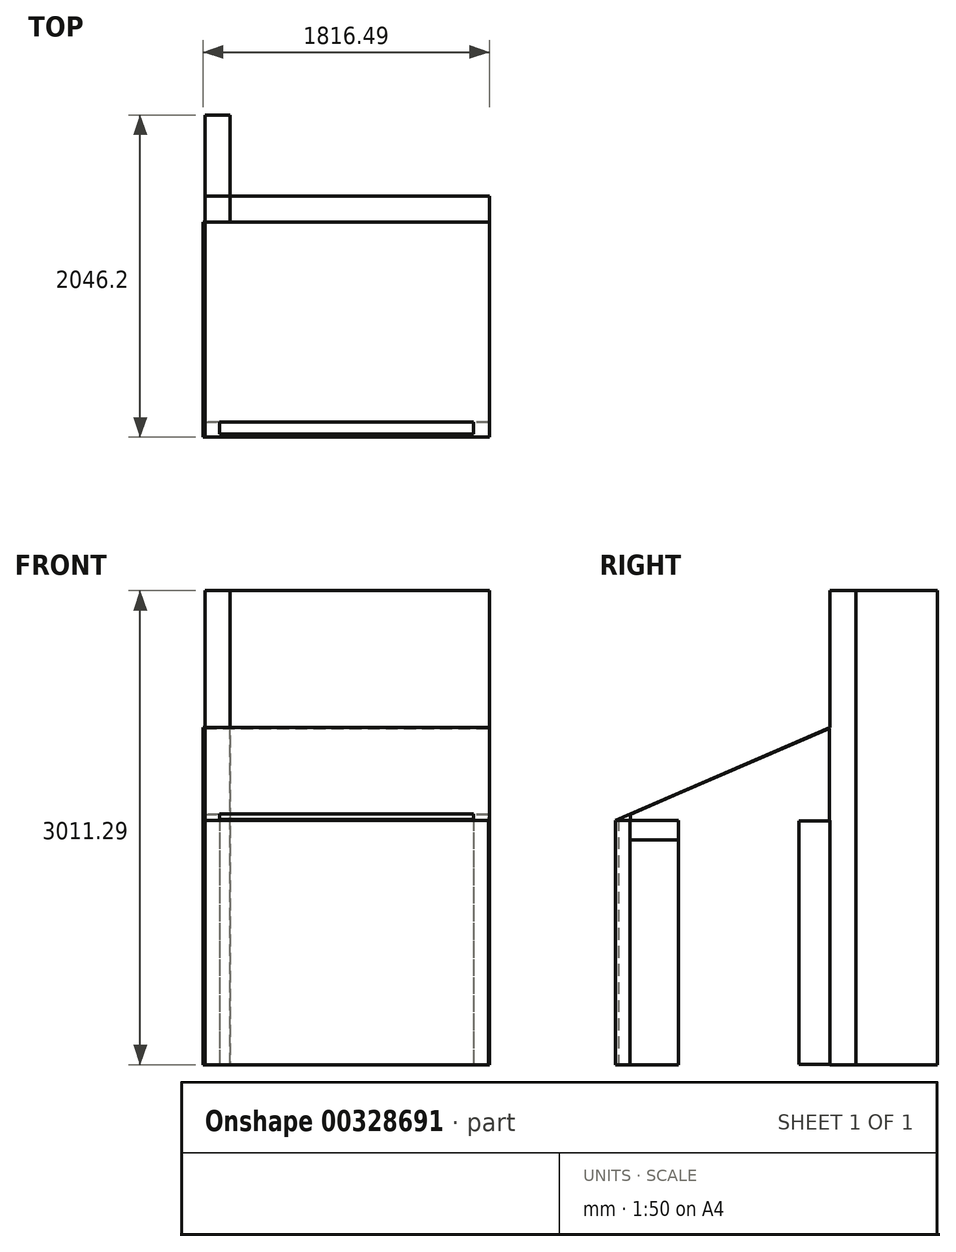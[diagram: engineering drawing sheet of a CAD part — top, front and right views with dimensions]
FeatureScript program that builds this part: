
annotation { "Feature Type Name" : "Feature", "Feature Type Description" : "" }
export const myFeature = defineFeature(function(context is Context, id is Id, definition is map)
    precondition{}
    {
        {
            var Q0;
            Q0=qCreatedBy(makeId("Right.planeOp"),FACE);
            var sketch = newSketch(context, id + "F0", { "sketchPlane" : qUnion([Q0])});
            skLineSegment(sketch, "E0.bottom", {"start": v(0, -290) * mm, "end": v(-95, -290) * mm});
            skLineSegment(sketch, "E0.left", {"start": v(0, -290) * mm, "end": v(0, 1300) * mm});
            skLineSegment(sketch, "E0.right", {"start": v(-95, -290) * mm, "end": v(-95, 1260) * mm});
            skLineSegment(sketch, "E1", {"start": v(-95, 1260) * mm, "end": v(-95, 1260) * mm});
            skLineSegment(sketch, "E2", {"start": v(0, 1300) * mm, "end": v(-95, 1260) * mm});
            skSolve(sketch);
        }
        {
            var Q0;
            Q0 = qSketchRegion(id + "F0", true);
            extrude(context, id + "F1", {"entities" : qUnion([Q0]), "depth" : 1800 * mm});
        }
        {
            var Q0;
            Q0=makeQuery(id+"F1.opExtrude","CAP_FACE",FACE,{"disambiguationData":[OSD([sQuery(id+"F0.wireOp",EDGE,"E0.bottom"),sQuery(id+"F0.wireOp",EDGE,"E0.left"),sQuery(id+"F0.wireOp",EDGE,"E0.right"),sQuery(id+"F0.wireOp",EDGE,"E2")])],"isStart":true});
            var sketch = newSketch(context, id + "F2", { "sketchPlane" : qUnion([Q0])});
            skPoint(sketch, "E3.end.orphan", {"position": v(95, -821.41) * mm});
            skPoint(sketch, "E3.start.orphan", {"position": v(-1270, -821.41) * mm});
            skLineSegment(sketch, "E4", {"start": v(-1270, -290) * mm, "end": v(-1270, 2721) * mm});
            skLineSegment(sketch, "E5", {"start": v(-1270, 2721) * mm, "end": v(-1951.2, 2721) * mm});
            skLineSegment(sketch, "E6", {"start": v(-1951.2, 2721) * mm, "end": v(-1951.2, -290) * mm});
            skLineSegment(sketch, "E7", {"start": v(-1951.2, -290) * mm, "end": v(-1270, -290) * mm});
            skLineSegment(sketch, "E8", {"start": v(95, 1260) * mm, "end": v(-1270, 1852.83) * mm});
            skPoint(sketch, "E9.end.orphan", {"position": v(-587.5, -290) * mm});
            skPoint(sketch, "E10.orphan", {"position": v(95, -290) * mm});
            skLineSegment(sketch, "E11", {"start": v(95, 1260) * mm, "end": v(0, 1260) * mm});
            skLineSegment(sketch, "E12", {"start": v(0, 1260) * mm, "end": v(-1270, 1260) * mm});
            skSolve(sketch);
        }
        {
            var Q0;
            {var subQ0=sQuery(id+"F2.wireOp",EDGE,"E11");Q0=makeQuery(id+"F2.imprint","IMPRINT",FACE,{"disambiguationData":[TD([[makeQuery(id+"F2.imprint","IMPRINT",EDGE,{"derivedFrom":subQ0}),1.0]])]});}
            var sketch = newSketch(context, id + "F3", { "sketchPlane" : qUnion([Q0])});
            skPoint(sketch, "E13.start.orphan", {"position": v(-1269.2, 1262.92) * mm});
            skLineSegment(sketch, "E14", {"start": v(-1270.6, 1381.92) * mm, "end": v(-1269.2, 1262.92) * mm});
            skPoint(sketch, "E15.end.orphan", {"position": v(-1302.17, 1381.92) * mm});
            skPoint(sketch, "E15.start.orphan", {"position": v(-1302.17, 1262.92) * mm});
            skLineSegment(sketch, "E16", {"start": v(-1270.6, 1381.92) * mm, "end": v(-1272, 1500.92) * mm});
            skLineSegment(sketch, "E17", {"start": v(-1272, 1500.92) * mm, "end": v(-1272, 1619.92) * mm});
            skLineSegment(sketch, "E18", {"start": v(-1272, 1619.92) * mm, "end": v(-1272, 1738.92) * mm});
            skLineSegment(sketch, "E19", {"start": v(-1272, 1738.92) * mm, "end": v(-1272, 1857.92) * mm});
            skLineSegment(sketch, "E20", {"start": v(-1269.2, 1262.92) * mm, "end": v(0, 1262.92) * mm});
            skLineSegment(sketch, "E21", {"start": v(0, 1262.92) * mm, "end": v(0, 1307.88) * mm});
            skLineSegment(sketch, "E22", {"start": v(-1272, 1857.92) * mm, "end": v(0, 1307.88) * mm});
            skLineSegment(sketch, "E23", {"start": v(-1270.6, 1381.92) * mm, "end": v(-171.23, 1381.92) * mm});
            skLineSegment(sketch, "E24", {"start": v(-1272, 1500.92) * mm, "end": v(-446.4, 1500.92) * mm});
            skLineSegment(sketch, "E25", {"start": v(-1272, 1619.92) * mm, "end": v(-721.6, 1619.92) * mm});
            skLineSegment(sketch, "E26", {"start": v(-1272, 1738.92) * mm, "end": v(-996.8, 1738.92) * mm});
            skLineSegment(sketch, "E27", {"start": v(334.75, -589.34) * mm, "end": v(334.75, -589.34) * mm});
            skLineSegment(sketch, "E28", {"start": v(95, -290.3) * mm, "end": v(-305, -290.3) * mm});
            skPoint(sketch, "E29.end.orphan", {"position": v(-505, -589.34) * mm});
            skLineSegment(sketch, "E30", {"start": v(-305, -290.3) * mm, "end": v(-305, 1262.92) * mm});
            skPoint(sketch, "E31.start.orphan", {"position": v(95, -622.61) * mm});
            skPoint(sketch, "E32.orphan", {"position": v(-505, -290.3) * mm});
            skLineSegment(sketch, "E33", {"start": v(95, -290.3) * mm, "end": v(95, -171.3) * mm});
            skLineSegment(sketch, "E34", {"start": v(95, -171.3) * mm, "end": v(95, -52.3) * mm});
            skLineSegment(sketch, "E35", {"start": v(95, -52.3) * mm, "end": v(95, 66.7) * mm});
            skLineSegment(sketch, "E36", {"start": v(95, 66.7) * mm, "end": v(95, 185.7) * mm});
            skLineSegment(sketch, "E37", {"start": v(95, 185.7) * mm, "end": v(95, 304.7) * mm});
            skLineSegment(sketch, "E38", {"start": v(95, 304.7) * mm, "end": v(95, 423.7) * mm});
            skLineSegment(sketch, "E39", {"start": v(95, 423.7) * mm, "end": v(95, 542.7) * mm});
            skLineSegment(sketch, "E40", {"start": v(95, 542.7) * mm, "end": v(95, 661.7) * mm});
            skLineSegment(sketch, "E41", {"start": v(95, 661.7) * mm, "end": v(95, 780.7) * mm});
            skLineSegment(sketch, "E42", {"start": v(95, 780.7) * mm, "end": v(95, 899.7) * mm});
            skLineSegment(sketch, "E43", {"start": v(95, 899.7) * mm, "end": v(95, 1018.7) * mm});
            skLineSegment(sketch, "E44", {"start": v(95, 1018.7) * mm, "end": v(95, 1137.7) * mm});
            skLineSegment(sketch, "E45", {"start": v(95, 1137.7) * mm, "end": v(95, 1256.7) * mm});
            skLineSegment(sketch, "E46", {"start": v(95, 1137.7) * mm, "end": v(-305, 1137.7) * mm});
            skLineSegment(sketch, "E47", {"start": v(95, 1018.7) * mm, "end": v(-305, 1018.7) * mm});
            skLineSegment(sketch, "E48", {"start": v(95, 899.7) * mm, "end": v(-305, 899.7) * mm});
            skLineSegment(sketch, "E49", {"start": v(95, 780.7) * mm, "end": v(-305, 780.7) * mm});
            skLineSegment(sketch, "E50", {"start": v(95, 661.7) * mm, "end": v(-305, 661.7) * mm});
            skLineSegment(sketch, "E51", {"start": v(95, 542.7) * mm, "end": v(-305, 542.7) * mm});
            skPoint(sketch, "E51.endSnap0", {"position": v(-305, 486.31) * mm});
            skLineSegment(sketch, "E52", {"start": v(95, 423.7) * mm, "end": v(-305, 423.7) * mm});
            skLineSegment(sketch, "E53", {"start": v(95, 304.7) * mm, "end": v(-305, 304.7) * mm});
            skLineSegment(sketch, "E54", {"start": v(95, 185.7) * mm, "end": v(-305, 185.7) * mm});
            skLineSegment(sketch, "E55", {"start": v(95, 66.7) * mm, "end": v(-305, 66.7) * mm});
            skLineSegment(sketch, "E56", {"start": v(95, -52.3) * mm, "end": v(-305, -52.3) * mm});
            skLineSegment(sketch, "E57", {"start": v(95, -171.3) * mm, "end": v(-305, -171.3) * mm});
            skLineSegment(sketch, "E58", {"start": v(-1270.61, -288.9) * mm, "end": v(-1070.61, -288.9) * mm});
            skLineSegment(sketch, "E59", {"start": v(-1070.61, -288.9) * mm, "end": v(-1070.61, 1262.92) * mm});
            skLineSegment(sketch, "E60", {"start": v(-1269.2, 1262.92) * mm, "end": v(-1269.2, 0) * mm});
            skLineSegment(sketch, "E61", {"start": v(-1269.2, 0) * mm, "end": v(-1270.61, -288.9) * mm});
            skLineSegment(sketch, "E62", {"start": v(-1070.61, -171.3) * mm, "end": v(-1270.04, -171.3) * mm});
            skLineSegment(sketch, "E63", {"start": v(-1070.61, -52.3) * mm, "end": v(-1269.46, -52.3) * mm});
            skLineSegment(sketch, "E64", {"start": v(-1070.61, 66.7) * mm, "end": v(-1269.2, 66.7) * mm});
            skLineSegment(sketch, "E65", {"start": v(-305, 185.7) * mm, "end": v(-305, 185.7) * mm});
            skLineSegment(sketch, "E66", {"start": v(-1070.61, 185.7) * mm, "end": v(-1269.2, 185.7) * mm});
            skLineSegment(sketch, "E67", {"start": v(-1070.61, 304.7) * mm, "end": v(-1269.2, 304.7) * mm});
            skLineSegment(sketch, "E68", {"start": v(-1070.61, 423.7) * mm, "end": v(-1269.2, 423.7) * mm});
            skLineSegment(sketch, "E69", {"start": v(-1070.61, 542.7) * mm, "end": v(-1269.2, 542.7) * mm});
            skPoint(sketch, "E69.endSnap0", {"position": v(-1269.2, 631.46) * mm});
            skLineSegment(sketch, "E70", {"start": v(-1070.61, 661.7) * mm, "end": v(-1269.2, 661.7) * mm});
            skLineSegment(sketch, "E71", {"start": v(-1070.61, 780.7) * mm, "end": v(-1269.2, 780.7) * mm});
            skLineSegment(sketch, "E72", {"start": v(-1070.61, 899.7) * mm, "end": v(-1269.2, 899.7) * mm});
            skLineSegment(sketch, "E73", {"start": v(-1070.61, 1018.7) * mm, "end": v(-1269.2, 1018.7) * mm});
            skLineSegment(sketch, "E74", {"start": v(-1070.61, 1137.7) * mm, "end": v(-1269.2, 1137.7) * mm});
            skSolve(sketch);
        }
        {
            var Q0;
            {var subQ2=sQuery(id+"F2.wireOp",EDGE,"E8");Q0=makeQuery(id+"F2.imprint","IMPRINT",FACE,{"disambiguationData":[TD([[makeQuery(id+"F2.imprint","IMPRINT",EDGE,{"derivedFrom":subQ2}),1.0]])]});}
            var Q1;
            {var subQ5=sQuery(id+"F3.wireOp",EDGE,"E74");Q1=makeQuery(id+"F3.imprint","IMPRINT",FACE,{"disambiguationData":[TD([[makeQuery(id+"F3.imprint","IMPRINT",EDGE,{"derivedFrom":subQ5}),-1.0]])]});}
            var Q2;
            {var subQ0=sQuery(id+"F3.wireOp",EDGE,"E71");Q2=makeQuery(id+"F3.imprint","IMPRINT",FACE,{"disambiguationData":[TD([[makeQuery(id+"F3.imprint","IMPRINT",EDGE,{"derivedFrom":subQ0}),-1.0]])]});}
            var Q3;
            {var subQ0=sQuery(id+"F3.wireOp",EDGE,"E73");Q3=makeQuery(id+"F3.imprint","IMPRINT",FACE,{"disambiguationData":[TD([[makeQuery(id+"F3.imprint","IMPRINT",EDGE,{"derivedFrom":subQ0}),-1.0]])]});}
            var Q4;
            {var subQ0=sQuery(id+"F3.wireOp",EDGE,"E72");Q4=makeQuery(id+"F3.imprint","IMPRINT",FACE,{"disambiguationData":[TD([[makeQuery(id+"F3.imprint","IMPRINT",EDGE,{"derivedFrom":subQ0}),-1.0]])]});}
            var Q5;
            {var subQ0=sQuery(id+"F3.wireOp",EDGE,"E69");Q5=makeQuery(id+"F3.imprint","IMPRINT",FACE,{"disambiguationData":[TD([[makeQuery(id+"F3.imprint","IMPRINT",EDGE,{"derivedFrom":subQ0}),-1.0]])]});}
            var Q6;
            {var subQ0=sQuery(id+"F3.wireOp",EDGE,"E70");Q6=makeQuery(id+"F3.imprint","IMPRINT",FACE,{"disambiguationData":[TD([[makeQuery(id+"F3.imprint","IMPRINT",EDGE,{"derivedFrom":subQ0}),-1.0]])]});}
            var Q7;
            {var subQ0=sQuery(id+"F3.wireOp",EDGE,"E68");Q7=makeQuery(id+"F3.imprint","IMPRINT",FACE,{"disambiguationData":[TD([[makeQuery(id+"F3.imprint","IMPRINT",EDGE,{"derivedFrom":subQ0}),-1.0]])]});}
            var Q8;
            {var subQ0=sQuery(id+"F3.wireOp",EDGE,"E67");Q8=makeQuery(id+"F3.imprint","IMPRINT",FACE,{"disambiguationData":[TD([[makeQuery(id+"F3.imprint","IMPRINT",EDGE,{"derivedFrom":subQ0}),-1.0]])]});}
            var Q9;
            {var subQ0=sQuery(id+"F3.wireOp",EDGE,"E66");Q9=makeQuery(id+"F3.imprint","IMPRINT",FACE,{"disambiguationData":[TD([[makeQuery(id+"F3.imprint","IMPRINT",EDGE,{"derivedFrom":subQ0}),-1.0]])]});}
            var Q10;
            {var subQ0=sQuery(id+"F3.wireOp",EDGE,"E64");Q10=makeQuery(id+"F3.imprint","IMPRINT",FACE,{"disambiguationData":[TD([[makeQuery(id+"F3.imprint","IMPRINT",EDGE,{"derivedFrom":subQ0}),-1.0]])]});}
            var Q11;
            {var subQ3=sQuery(id+"F3.wireOp",EDGE,"E63");Q11=makeQuery(id+"F3.imprint","IMPRINT",FACE,{"disambiguationData":[TD([[makeQuery(id+"F3.imprint","IMPRINT",EDGE,{"derivedFrom":subQ3}),-1.0]])]});}
            var Q12;
            {var subQ0=sQuery(id+"F3.wireOp",EDGE,"E62");Q12=makeQuery(id+"F3.imprint","IMPRINT",FACE,{"disambiguationData":[TD([[makeQuery(id+"F3.imprint","IMPRINT",EDGE,{"derivedFrom":subQ0}),-1.0]])]});}
            var Q13;
            {var subQ0=sQuery(id+"F3.wireOp",EDGE,"E58");Q13=makeQuery(id+"F3.imprint","IMPRINT",FACE,{"disambiguationData":[TD([[makeQuery(id+"F3.imprint","IMPRINT",EDGE,{"derivedFrom":subQ0}),1.0]])]});}
            var Q14;
            {var subQ3=sQuery(id+"F3.wireOp",EDGE,"E28");Q14=makeQuery(id+"F3.imprint","IMPRINT",FACE,{"disambiguationData":[TD([[makeQuery(id+"F3.imprint","IMPRINT",EDGE,{"derivedFrom":subQ3}),-1.0]])]});}
            var Q15;
            {var subQ0=sQuery(id+"F3.wireOp",EDGE,"E56");var subQ1=sQuery(id+"F3.wireOp",EDGE,"E30");var subQ2=makeQuery(id+"F3.imprint","INTERSECT",VERTEX,{"derivedFrom":[subQ1,subQ0]});Q15=makeQuery(id+"F3.imprint","IMPRINT",FACE,{"disambiguationData":[TD([[makeQuery(id+"F3.imprint","IMPRINT",EDGE,{"disambiguationData":[TD([[subQ2,1.0]])],"derivedFrom":subQ1}),-1.0]])]});}
            var Q16;
            {var subQ0=sQuery(id+"F3.wireOp",EDGE,"E55");var subQ1=sQuery(id+"F3.wireOp",EDGE,"E30");var subQ2=makeQuery(id+"F3.imprint","INTERSECT",VERTEX,{"derivedFrom":[subQ1,subQ0]});Q16=makeQuery(id+"F3.imprint","IMPRINT",FACE,{"disambiguationData":[TD([[makeQuery(id+"F3.imprint","IMPRINT",EDGE,{"disambiguationData":[TD([[subQ2,1.0]])],"derivedFrom":subQ1}),-1.0]])]});}
            var Q17;
            {var subQ0=sQuery(id+"F3.wireOp",EDGE,"E54");var subQ1=sQuery(id+"F3.wireOp",EDGE,"E30");var subQ2=makeQuery(id+"F3.imprint","INTERSECT",VERTEX,{"derivedFrom":[subQ1,subQ0]});Q17=makeQuery(id+"F3.imprint","IMPRINT",FACE,{"disambiguationData":[TD([[makeQuery(id+"F3.imprint","IMPRINT",EDGE,{"disambiguationData":[TD([[subQ2,1.0]])],"derivedFrom":subQ1}),-1.0]])]});}
            var Q18;
            {var subQ0=sQuery(id+"F3.wireOp",EDGE,"E53");var subQ1=sQuery(id+"F3.wireOp",EDGE,"E30");var subQ2=makeQuery(id+"F3.imprint","INTERSECT",VERTEX,{"derivedFrom":[subQ1,subQ0]});Q18=makeQuery(id+"F3.imprint","IMPRINT",FACE,{"disambiguationData":[TD([[makeQuery(id+"F3.imprint","IMPRINT",EDGE,{"disambiguationData":[TD([[subQ2,1.0]])],"derivedFrom":subQ1}),-1.0]])]});}
            var Q19;
            {var subQ0=sQuery(id+"F3.wireOp",EDGE,"E52");var subQ1=sQuery(id+"F3.wireOp",EDGE,"E30");var subQ2=makeQuery(id+"F3.imprint","INTERSECT",VERTEX,{"derivedFrom":[subQ1,subQ0]});Q19=makeQuery(id+"F3.imprint","IMPRINT",FACE,{"disambiguationData":[TD([[makeQuery(id+"F3.imprint","IMPRINT",EDGE,{"disambiguationData":[TD([[subQ2,1.0]])],"derivedFrom":subQ1}),-1.0]])]});}
            var Q20;
            {var subQ0=sQuery(id+"F3.wireOp",EDGE,"E51");var subQ1=sQuery(id+"F3.wireOp",EDGE,"E30");var subQ2=makeQuery(id+"F3.imprint","INTERSECT",VERTEX,{"derivedFrom":[subQ1,subQ0]});Q20=makeQuery(id+"F3.imprint","IMPRINT",FACE,{"disambiguationData":[TD([[makeQuery(id+"F3.imprint","IMPRINT",EDGE,{"disambiguationData":[TD([[subQ2,1.0]])],"derivedFrom":subQ1}),-1.0]])]});}
            var Q21;
            {var subQ0=sQuery(id+"F3.wireOp",EDGE,"E50");var subQ1=sQuery(id+"F3.wireOp",EDGE,"E30");var subQ2=makeQuery(id+"F3.imprint","INTERSECT",VERTEX,{"derivedFrom":[subQ1,subQ0]});Q21=makeQuery(id+"F3.imprint","IMPRINT",FACE,{"disambiguationData":[TD([[makeQuery(id+"F3.imprint","IMPRINT",EDGE,{"disambiguationData":[TD([[subQ2,1.0]])],"derivedFrom":subQ1}),-1.0]])]});}
            var Q22;
            {var subQ0=sQuery(id+"F3.wireOp",EDGE,"E48");var subQ1=sQuery(id+"F3.wireOp",EDGE,"E30");var subQ2=makeQuery(id+"F3.imprint","INTERSECT",VERTEX,{"derivedFrom":[subQ1,subQ0]});Q22=makeQuery(id+"F3.imprint","IMPRINT",FACE,{"disambiguationData":[TD([[makeQuery(id+"F3.imprint","IMPRINT",EDGE,{"disambiguationData":[TD([[subQ2,1.0]])],"derivedFrom":subQ1}),-1.0]])]});}
            var Q23;
            {var subQ0=sQuery(id+"F3.wireOp",EDGE,"E47");var subQ1=sQuery(id+"F3.wireOp",EDGE,"E30");var subQ2=makeQuery(id+"F3.imprint","INTERSECT",VERTEX,{"derivedFrom":[subQ1,subQ0]});Q23=makeQuery(id+"F3.imprint","IMPRINT",FACE,{"disambiguationData":[TD([[makeQuery(id+"F3.imprint","IMPRINT",EDGE,{"disambiguationData":[TD([[subQ2,1.0]])],"derivedFrom":subQ1}),-1.0]])]});}
            var Q24;
            {var subQ0=sQuery(id+"F3.wireOp",EDGE,"E49");var subQ1=sQuery(id+"F3.wireOp",EDGE,"E30");var subQ2=makeQuery(id+"F3.imprint","INTERSECT",VERTEX,{"derivedFrom":[subQ1,subQ0]});Q24=makeQuery(id+"F3.imprint","IMPRINT",FACE,{"disambiguationData":[TD([[makeQuery(id+"F3.imprint","IMPRINT",EDGE,{"disambiguationData":[TD([[subQ2,1.0]])],"derivedFrom":subQ1}),-1.0]])]});}
            var Q25;
            {var subQ0=sQuery(id+"F3.wireOp",EDGE,"E46");var subQ1=sQuery(id+"F3.wireOp",EDGE,"E30");var subQ2=makeQuery(id+"F3.imprint","INTERSECT",VERTEX,{"derivedFrom":[subQ1,subQ0]});Q25=makeQuery(id+"F3.imprint","IMPRINT",FACE,{"disambiguationData":[TD([[makeQuery(id+"F3.imprint","IMPRINT",EDGE,{"disambiguationData":[TD([[subQ2,1.0]])],"derivedFrom":subQ1}),-1.0]])]});}
            extrude(context, id + "F4", {"entities" : qUnion([Q0, Q1, Q2, Q3, Q4, Q5, Q6, Q7, Q8, Q9, Q10, Q11, Q12, Q13, Q14, Q15, Q16, Q17, Q18, Q19, Q20, Q21, Q22, Q23, Q24, Q25]), "depth" : 10 * mm});
        }
        {
            var Q0;
            Q0=makeQuery(id+"F4.opExtrude","CAP_FACE",FACE,{"disambiguationData":[OSD([sQuery(id+"F0.wireOp",EDGE,"E0.left"),sQuery(id+"F0.wireOp",EDGE,"E2"),sQuery(id+"F2.wireOp",EDGE,"E4"),sQuery(id+"F2.wireOp",EDGE,"E8"),sQuery(id+"F2.wireOp",EDGE,"E12")])],"isStart":false});
            var sketch = newSketch(context, id + "F5", { "sketchPlane" : qUnion([Q0])});
            skLineSegment(sketch, "E75", {"start": v(-305.24, 1137.73) * mm, "end": v(-305.24, 1260) * mm});
            skLineSegment(sketch, "E76", {"start": v(-305.24, 1260) * mm, "end": v(0, 1260) * mm});
            skLineSegment(sketch, "E77", {"start": v(0, 1260) * mm, "end": v(0, 1138.9) * mm});
            skLineSegment(sketch, "E78", {"start": v(0, 1138.9) * mm, "end": v(-305.24, 1137.73) * mm});
            skSolve(sketch);
        }
        {
            var Q0;
            Q0=makeQuery(id+"F5.imprint","IMPRINT",FACE,{"disambiguationData":[TD([[makeQuery(id+"F5.imprint","IMPRINT",EDGE,{"derivedFrom":sQuery(id+"F5.wireOp",EDGE,"E75")}),-1.0]])]});
            extrude(context, id + "F6", {"entities" : qUnion([Q0]), "operationType" : NewBodyOperationType.ADD, "oppositeDirection" : true, "depth" : 10 * mm});
        }
        {
            var Q0;
            {var subQ0=sQuery(id+"F2.wireOp",EDGE,"E5");Q0=makeQuery(id+"F2.imprint","IMPRINT",FACE,{"disambiguationData":[TD([[makeQuery(id+"F2.imprint","IMPRINT",EDGE,{"derivedFrom":subQ0}),1.0]])]});}
            var Q1;
            Q1 = qSketchRegion(id + "F2", true);
            extrude(context, id + "F7", {"entities" : qUnion([Q0, Q1]), "oppositeDirection" : true, "depth" : 1806.5 * mm});
        }
        {
            var Q0;
            Q0=makeQuery(id+"F7.opExtrude","CAP_FACE",FACE,{"disambiguationData":[OSD([sQuery(id+"F2.wireOp",EDGE,"E4"),sQuery(id+"F2.wireOp",EDGE,"E5"),sQuery(id+"F2.wireOp",EDGE,"E6"),sQuery(id+"F2.wireOp",EDGE,"E7"),sQuery(id+"F2.wireOp",EDGE,"E8"),sQuery(id+"F2.wireOp",EDGE,"E11"),sQuery(id+"F2.wireOp",EDGE,"E12")])],"isStart":false});
            var sketch = newSketch(context, id + "F8", { "sketchPlane" : qUnion([Q0])});
            skLineSegment(sketch, "E79", {"start": v(305.91, 1258.1) * mm, "end": v(305.91, 1261.87) * mm});
            skLineSegment(sketch, "E80.right", {"start": v(1266.17, 1261.87) * mm, "end": v(1266.17, 1289.45) * mm});
            skLineSegment(sketch, "E81", {"start": v(1266.17, 1289.45) * mm, "end": v(1266.17, 1648.2) * mm});
            skLineSegment(sketch, "E82", {"start": v(1266.17, 1648.2) * mm, "end": v(1266.17, 1648.2) * mm});
            skLineSegment(sketch, "E83", {"start": v(1266.17, 1648.2) * mm, "end": v(1266.17, 1803.9) * mm});
            skLineSegment(sketch, "E84", {"start": v(1266.17, 1803.9) * mm, "end": v(1266.17, 1803.9) * mm});
            skLineSegment(sketch, "E85", {"start": v(1266.17, 1803.9) * mm, "end": v(1266.17, 1846.34) * mm});
            skLineSegment(sketch, "E86", {"start": v(1266.17, 1846.34) * mm, "end": v(1266.17, 1846.34) * mm});
            skLineSegment(sketch, "E87", {"start": v(1266.17, 1846.34) * mm, "end": v(1266.17, 1849.95) * mm});
            skLineSegment(sketch, "E88", {"start": v(1266.17, 1846.34) * mm, "end": v(305.91, 1433.16) * mm});
            skLineSegment(sketch, "E89", {"start": v(305.91, 1258.1) * mm, "end": v(379.95, 1258.1) * mm});
            skLineSegment(sketch, "E90", {"start": v(379.95, 1258.1) * mm, "end": v(522.25, 1258.1) * mm});
            skLineSegment(sketch, "E91", {"start": v(522.25, 1258.1) * mm, "end": v(522.25, 1258.1) * mm});
            skLineSegment(sketch, "E92", {"start": v(522.25, 1258.1) * mm, "end": v(570.38, 1258.1) * mm});
            skLineSegment(sketch, "E93", {"start": v(570.38, 1258.1) * mm, "end": v(747.25, 1258.1) * mm});
            skLineSegment(sketch, "E94", {"start": v(305.91, 1433.16) * mm, "end": v(305.91, 1258.1) * mm});
            skLineSegment(sketch, "E95", {"start": v(916.76, 1258.1) * mm, "end": v(747.25, 1258.1) * mm});
            skLineSegment(sketch, "E96", {"start": v(916.76, 1258.1) * mm, "end": v(1097.19, 1258.1) * mm});
            skLineSegment(sketch, "E97", {"start": v(1097.19, 1258.1) * mm, "end": v(1266.17, 1258.1) * mm});
            skLineSegment(sketch, "E98", {"start": v(1266.17, 1261.87) * mm, "end": v(1266.17, 1258.1) * mm});
            skSolve(sketch);
        }
        {
            var Q0;
            Q0 = qSketchRegion(id + "F8", true);
            var Q1;
            {var subQ5=sQuery(id+"F8.wireOp",EDGE,"E80.right");Q1=makeQuery(id+"F8.imprint","IMPRINT",FACE,{"disambiguationData":[TD([[makeQuery(id+"F8.imprint","IMPRINT",EDGE,{"derivedFrom":subQ5}),1.0]])]});}
            extrude(context, id + "F9", {"entities" : qUnion([Q0, Q1]), "operationType" : NewBodyOperationType.REMOVE, "oppositeDirection" : true, "depth" : 2295.18 * mm});
        }
        {
            var Q0;
            Q0=makeQuery(id+"F7.opExtrude","CAP_FACE",FACE,{"disambiguationData":[OSD([sQuery(id+"F2.wireOp",EDGE,"E4"),sQuery(id+"F2.wireOp",EDGE,"E5"),sQuery(id+"F2.wireOp",EDGE,"E6"),sQuery(id+"F2.wireOp",EDGE,"E7"),sQuery(id+"F2.wireOp",EDGE,"E8"),sQuery(id+"F2.wireOp",EDGE,"E11"),sQuery(id+"F2.wireOp",EDGE,"E12")])],"isStart":false});
            var sketch = newSketch(context, id + "F10", { "sketchPlane" : qUnion([Q0])});
            skLineSegment(sketch, "E99", {"start": v(305.91, 1433.16) * mm, "end": v(202.21, 1388.12) * mm});
            skLineSegment(sketch, "E100", {"start": v(202.21, 1388.12) * mm, "end": v(8.54, 1304) * mm});
            skLineSegment(sketch, "E101", {"start": v(8.54, 1304) * mm, "end": v(8.54, 1304) * mm});
            skLineSegment(sketch, "E102", {"start": v(8.54, 1304) * mm, "end": v(0.9, 1300.68) * mm});
            skLineSegment(sketch, "E103", {"start": v(0.9, 1300.68) * mm, "end": v(0.9, 1253.51) * mm});
            skLineSegment(sketch, "E104", {"start": v(305.91, 1433.16) * mm, "end": v(305.91, 1253.51) * mm});
            skLineSegment(sketch, "E105", {"start": v(305.91, 1253.51) * mm, "end": v(0.9, 1253.51) * mm});
            skSolve(sketch);
        }
        {
            var Q0;
            {var subQ7=sQuery(id+"F10.wireOp",EDGE,"E99");Q0=makeQuery(id+"F10.imprint","IMPRINT",FACE,{"disambiguationData":[TD([[makeQuery(id+"F10.imprint","IMPRINT",EDGE,{"derivedFrom":subQ7}),1.0]])]});}
            extrude(context, id + "F11", {"entities" : qUnion([Q0]), "operationType" : NewBodyOperationType.REMOVE, "oppositeDirection" : true, "depth" : 1985.6 * mm});
        }
        {
            var Q0;
            {var subQ0=sQuery(id+"F2.wireOp",EDGE,"E5");Q0=makeQuery(id+"F2.imprint","IMPRINT",FACE,{"disambiguationData":[TD([[makeQuery(id+"F2.imprint","IMPRINT",EDGE,{"derivedFrom":subQ0}),1.0]])]});}
            var sketch = newSketch(context, id + "F12", { "sketchPlane" : qUnion([Q0])});
            skLineSegment(sketch, "E106.bottom", {"start": v(-2153.87, -657.47) * mm, "end": v(-1434.67, -657.47) * mm});
            skLineSegment(sketch, "E106.top", {"start": v(-2153.87, 3181.57) * mm, "end": v(-1434.67, 3181.57) * mm});
            skLineSegment(sketch, "E106.left", {"start": v(-2153.87, -657.47) * mm, "end": v(-2153.87, 3181.57) * mm});
            skLineSegment(sketch, "E106.right", {"start": v(-1434.67, -657.47) * mm, "end": v(-1434.67, 3181.57) * mm});
            skSolve(sketch);
        }
        {
            var Q0;
            Q0 = qSketchRegion(id + "F12", true);
            extrude(context, id + "F13", {"entities" : qUnion([Q0]), "operationType" : NewBodyOperationType.REMOVE, "oppositeDirection" : true, "depth" : 2175.2 * mm});
        }
        {
            var Q0;
            {var subQ0=sQuery(id+"F2.wireOp",EDGE,"E5");Q0=makeQuery(id+"F2.imprint","IMPRINT",FACE,{"disambiguationData":[TD([[makeQuery(id+"F2.imprint","IMPRINT",EDGE,{"derivedFrom":subQ0}),1.0]])]});}
            extrude(context, id + "F14", {"entities" : qUnion([Q0]), "oppositeDirection" : true, "depth" : 160.8 * mm});
        }
        {
            var Q0;
            Q0=makeQuery(id+"F1.opExtrude","SWEPT_FACE",FACE,{"disambiguationData":[OSD([sQuery(id+"F0.wireOp",EDGE,"E0.bottom")])]});
            var sketch = newSketch(context, id + "F15", { "sketchPlane" : qUnion([Q0])});
            skLineSegment(sketch, "E107", {"start": v(0, 0) * mm, "end": v(95, 0) * mm});
            skLineSegment(sketch, "E108", {"start": v(1800, 0) * mm, "end": v(1705, 0) * mm});
            skLineSegment(sketch, "E109.bottom", {"start": v(95, 0) * mm, "end": v(1705, 0) * mm});
            skLineSegment(sketch, "E109.top", {"start": v(95, 74.89) * mm, "end": v(1705, 74.89) * mm});
            skLineSegment(sketch, "E109.left", {"start": v(95, 0) * mm, "end": v(95, 74.89) * mm});
            skLineSegment(sketch, "E109.right", {"start": v(1705, 0) * mm, "end": v(1705, 74.89) * mm});
            skSolve(sketch);
        }
        {
            var Q0;
            Q0=makeQuery(id+"F15.imprint","IMPRINT",FACE,{"disambiguationData":[TD([[makeQuery(id+"F15.imprint","IMPRINT",EDGE,{"derivedFrom":sQuery(id+"F15.wireOp",EDGE,"E109.bottom")}),-1.0]])]});
            extrude(context, id + "F16", {"entities" : qUnion([Q0]), "operationType" : NewBodyOperationType.REMOVE, "oppositeDirection" : true, "depth" : 2483.98 * mm});
        }
    });
